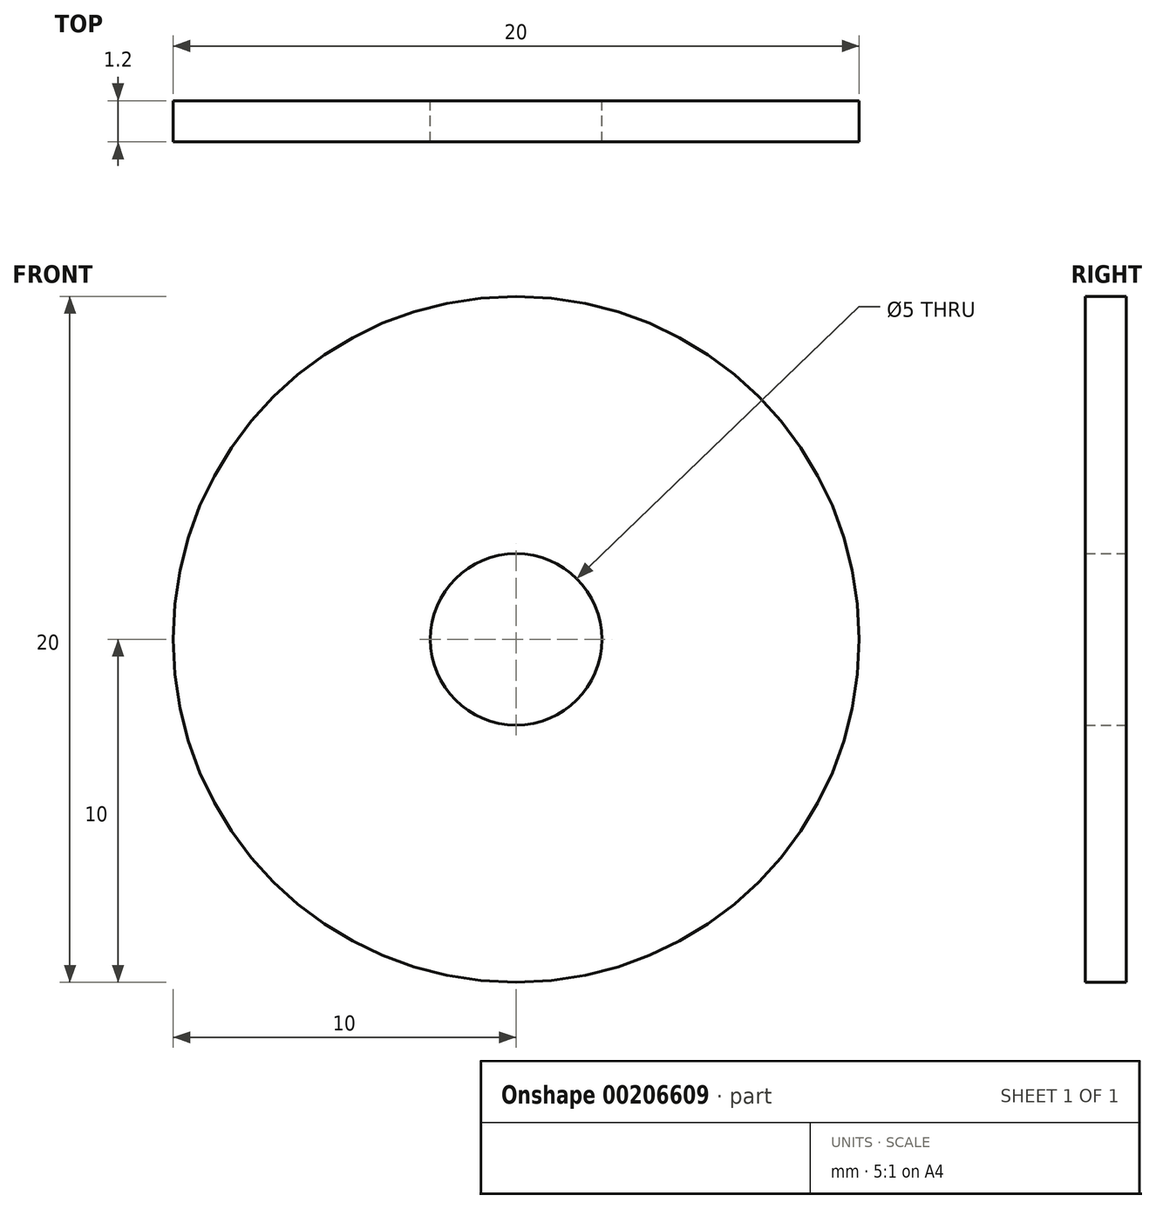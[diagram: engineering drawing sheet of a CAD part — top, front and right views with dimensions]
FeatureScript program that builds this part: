
annotation { "Feature Type Name" : "Feature", "Feature Type Description" : "" }
export const myFeature = defineFeature(function(context is Context, id is Id, definition is map)
    precondition{}
    {
        {
            var Q0;
            Q0=qCreatedBy(makeId("Front.planeOp"),FACE);
            var sketch = newSketch(context, id + "F0", { "sketchPlane" : qUnion([Q0])});
            skCircle(sketch, "E0", {"center": v(0, 0) * mm, "radius": 2.5 * mm});
            skCircle(sketch, "E1", {"center": v(0, 0) * mm, "radius": 10 * mm});
            skSolve(sketch);
        }
        {
            var Q0;
            Q0=makeQuery(id+"F0.imprint","IMPRINT",FACE,{"disambiguationData":[TD([[makeQuery(id+"F0.imprint","IMPRINT",EDGE,{"derivedFrom":sQuery(id+"F0.wireOp",EDGE,"E0")}),-1.0]])]});
            extrude(context, id + "F1", {"entities" : qUnion([Q0]), "depth" : 1.2 * mm});
        }
    });
